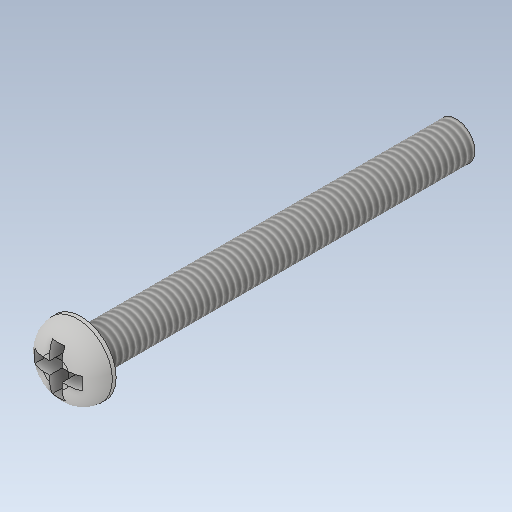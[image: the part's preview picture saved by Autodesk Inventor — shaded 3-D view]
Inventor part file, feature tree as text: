
AUTODESK INVENTOR PART (.ipt)
format: ipt  version: 2020 (Build 240168000, 168)  size: 165,376 bytes
history: native  units: mm
features: extrude x3, sketch x3, other x1, fillet x1, thread x1
ambient origin geometry x8: Origin, YZ Plane, XZ Plane, XY Plane, X Axis, Y Axis, Z Axis, Center Point
bodies: Body1 (feature_tree)
feature tree (9):
  other  "Твердое тело1"
  extrude  "Выдавливание1"  Depth=30.0mm TaperAngle=0.0deg
  extrude  "Выдавливание2"  Depth=2.0mm TaperAngle=0.0deg
  fillet  "Сопряжение1"  Radius=1.7mm
  extrude  "Выдавливание3"  Depth=1.5mm TaperAngle=0.0deg
  thread  "Резьба1"
  sketch  "Эскиз1"
  sketch  "Эскиз2"
  sketch  "Эскиз3"
